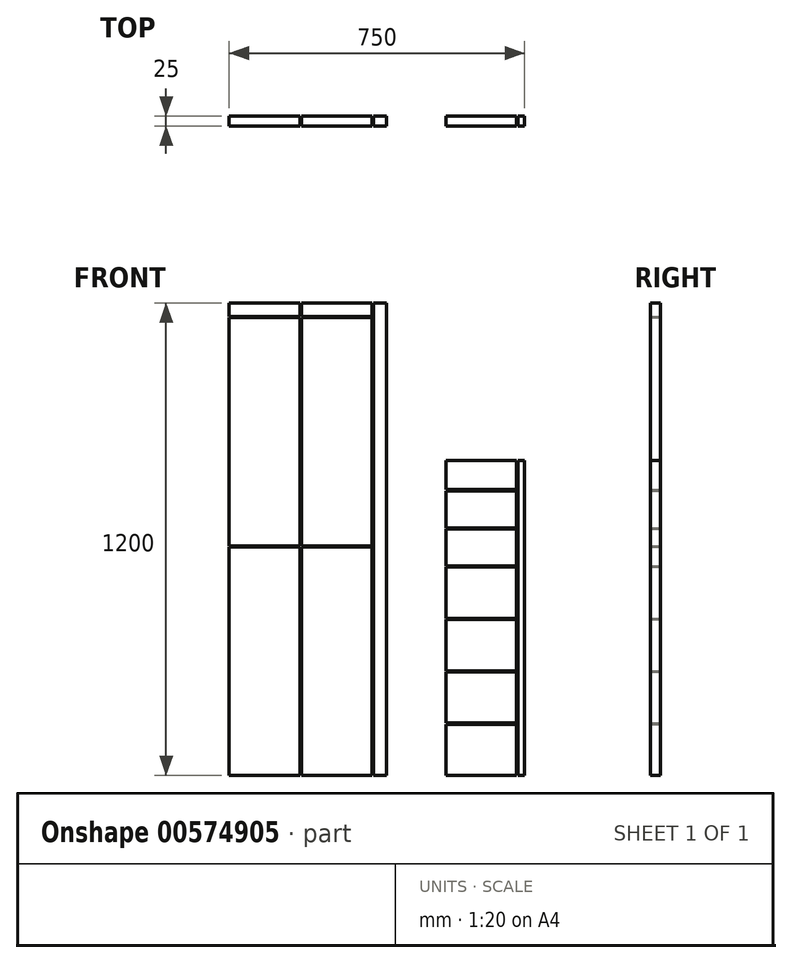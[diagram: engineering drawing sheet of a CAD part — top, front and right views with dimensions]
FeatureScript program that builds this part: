
annotation { "Feature Type Name" : "Feature", "Feature Type Description" : "" }
export const myFeature = defineFeature(function(context is Context, id is Id, definition is map)
    precondition{}
    {
        {
            var Q0;
            Q0=qCreatedBy(makeId("Front.planeOp"),FACE);
            var sketch = newSketch(context, id + "F0", { "sketchPlane" : qUnion([Q0])});
            skLineSegment(sketch, "E0.bottom", {"start": v(0, 0) * mm, "end": v(400, 0) * mm});
            skLineSegment(sketch, "E0.top", {"start": v(0, 1200) * mm, "end": v(400, 1200) * mm});
            skLineSegment(sketch, "E0.left", {"start": v(0, 0) * mm, "end": v(0, 1200) * mm});
            skLineSegment(sketch, "E0.right", {"start": v(400, 0) * mm, "end": v(400, 1200) * mm});
            skLineSegment(sketch, "E1", {"start": v(180, 0) * mm, "end": v(180, 1200) * mm});
            skLineSegment(sketch, "E2.0", {"start": v(183, 0) * mm, "end": v(183, 1200) * mm});
            skLineSegment(sketch, "E3.0", {"start": v(363, 0) * mm, "end": v(363, 1200) * mm});
            skLineSegment(sketch, "E4.0", {"start": v(366, 0) * mm, "end": v(366, 1200) * mm});
            skLineSegment(sketch, "E5", {"start": v(0, 580) * mm, "end": v(366, 580) * mm});
            skLineSegment(sketch, "E6.0", {"start": v(0, 583) * mm, "end": v(366, 583) * mm});
            skLineSegment(sketch, "E7.0", {"start": v(0, 1163) * mm, "end": v(366, 1163) * mm});
            skLineSegment(sketch, "E8.0", {"start": v(0, 1166) * mm, "end": v(366, 1166) * mm});
            skSolve(sketch);
        }
        {
            var Q0;
            {var subQ0=sQuery(id+"F0.wireOp",EDGE,"E6.0");var subQ1=sQuery(id+"F0.wireOp",EDGE,"E0.left");var subQ2=makeQuery(id+"F0.imprint","INTERSECT",VERTEX,{"derivedFrom":[subQ1,subQ0]});Q0=makeQuery(id+"F0.imprint","IMPRINT",FACE,{"disambiguationData":[TD([[makeQuery(id+"F0.imprint","IMPRINT",EDGE,{"disambiguationData":[TD([[subQ2,-1.0]])],"derivedFrom":subQ1}),-1.0]])]});}
            var Q1;
            {var subQ0=sQuery(id+"F0.wireOp",EDGE,"E6.0");var subQ1=sQuery(id+"F0.wireOp",EDGE,"E2.0");var subQ2=makeQuery(id+"F0.imprint","INTERSECT",VERTEX,{"derivedFrom":[subQ1,subQ0]});Q1=makeQuery(id+"F0.imprint","IMPRINT",FACE,{"disambiguationData":[TD([[makeQuery(id+"F0.imprint","IMPRINT",EDGE,{"disambiguationData":[TD([[subQ2,-1.0]])],"derivedFrom":subQ1}),-1.0]])]});}
            var Q2;
            {var subQ0=sQuery(id+"F0.wireOp",EDGE,"E0.left");var subQ1=sQuery(id+"F0.wireOp",EDGE,"E0.bottom");var subQ2=makeQuery(id+"F0.imprint","INTERSECT",VERTEX,{"derivedFrom":[subQ1,subQ0]});Q2=makeQuery(id+"F0.imprint","IMPRINT",FACE,{"disambiguationData":[TD([[makeQuery(id+"F0.imprint","IMPRINT",EDGE,{"disambiguationData":[TD([[subQ2,-1.0]])],"derivedFrom":subQ1}),1.0]])]});}
            var Q3;
            {var subQ0=sQuery(id+"F0.wireOp",EDGE,"E2.0");var subQ1=sQuery(id+"F0.wireOp",EDGE,"E0.bottom");var subQ2=makeQuery(id+"F0.imprint","INTERSECT",VERTEX,{"derivedFrom":[subQ1,subQ0]});Q3=makeQuery(id+"F0.imprint","IMPRINT",FACE,{"disambiguationData":[TD([[makeQuery(id+"F0.imprint","IMPRINT",EDGE,{"disambiguationData":[TD([[subQ2,-1.0]])],"derivedFrom":subQ1}),1.0]])]});}
            var Q4;
            {var subQ0=sQuery(id+"F0.wireOp",EDGE,"E0.left");var subQ1=sQuery(id+"F0.wireOp",EDGE,"E0.top");var subQ2=makeQuery(id+"F0.imprint","INTERSECT",VERTEX,{"derivedFrom":[subQ1,subQ0]});Q4=makeQuery(id+"F0.imprint","IMPRINT",FACE,{"disambiguationData":[TD([[makeQuery(id+"F0.imprint","IMPRINT",EDGE,{"disambiguationData":[TD([[subQ2,-1.0]])],"derivedFrom":subQ1}),-1.0]])]});}
            var Q5;
            {var subQ0=sQuery(id+"F0.wireOp",EDGE,"E2.0");var subQ1=sQuery(id+"F0.wireOp",EDGE,"E0.top");var subQ2=makeQuery(id+"F0.imprint","INTERSECT",VERTEX,{"derivedFrom":[subQ1,subQ0]});Q5=makeQuery(id+"F0.imprint","IMPRINT",FACE,{"disambiguationData":[TD([[makeQuery(id+"F0.imprint","IMPRINT",EDGE,{"disambiguationData":[TD([[subQ2,-1.0]])],"derivedFrom":subQ1}),-1.0]])]});}
            var Q6;
            {var subQ4=sQuery(id+"F0.wireOp",EDGE,"E0.right");Q6=makeQuery(id+"F0.imprint","IMPRINT",FACE,{"disambiguationData":[TD([[makeQuery(id+"F0.imprint","IMPRINT",EDGE,{"derivedFrom":subQ4}),1.0]])]});}
            extrude(context, id + "F1", {"entities" : qUnion([Q0, Q1, Q2, Q3, Q4, Q5, Q6]), "depth" : 25 * mm, "offsetDistance" : 25 * mm});
        }
        {
            var Q0;
            Q0=qCreatedBy(makeId("Front.planeOp"),FACE);
            var sketch = newSketch(context, id + "F2", { "sketchPlane" : qUnion([Q0])});
            skLineSegment(sketch, "E9.bottom", {"start": v(550, 0) * mm, "end": v(750, 0) * mm});
            skLineSegment(sketch, "E9.top", {"start": v(550, 800) * mm, "end": v(750, 800) * mm});
            skLineSegment(sketch, "E9.left", {"start": v(550, 0) * mm, "end": v(550, 800) * mm});
            skLineSegment(sketch, "E9.right", {"start": v(750, 0) * mm, "end": v(750, 800) * mm});
            skLineSegment(sketch, "E10.0", {"start": v(730, 0) * mm, "end": v(730, 800) * mm});
            skLineSegment(sketch, "E11", {"start": v(550, 130) * mm, "end": v(730, 130) * mm});
            skLineSegment(sketch, "E12.0", {"start": v(550, 133) * mm, "end": v(730, 133) * mm});
            skLineSegment(sketch, "E13.0", {"start": v(550, 263) * mm, "end": v(730, 263) * mm});
            skLineSegment(sketch, "E14.0", {"start": v(550, 266) * mm, "end": v(730, 266) * mm});
            skLineSegment(sketch, "E15.0", {"start": v(550, 396) * mm, "end": v(730, 396) * mm});
            skLineSegment(sketch, "E16.0", {"start": v(550, 399) * mm, "end": v(730, 399) * mm});
            skLineSegment(sketch, "E17.0", {"start": v(550, 529) * mm, "end": v(730, 529) * mm});
            skLineSegment(sketch, "E18.0", {"start": v(550, 532) * mm, "end": v(730, 532) * mm});
            skLineSegment(sketch, "E19.0", {"start": v(550, 626) * mm, "end": v(730, 626) * mm});
            skLineSegment(sketch, "E20.0", {"start": v(550, 629) * mm, "end": v(730, 629) * mm});
            skLineSegment(sketch, "E21.0", {"start": v(550, 723) * mm, "end": v(730, 723) * mm});
            skLineSegment(sketch, "E22.0", {"start": v(550, 726) * mm, "end": v(730, 726) * mm});
            skLineSegment(sketch, "E23.0", {"start": v(733, 0) * mm, "end": v(733, 800) * mm});
            skSolve(sketch);
        }
        {
            var Q0;
            {var subQ5=sQuery(id+"F2.wireOp",EDGE,"E11");Q0=makeQuery(id+"F2.imprint","IMPRINT",FACE,{"disambiguationData":[TD([[makeQuery(id+"F2.imprint","IMPRINT",EDGE,{"derivedFrom":subQ5}),-1.0]])]});}
            var Q1;
            {var subQ0=sQuery(id+"F2.wireOp",EDGE,"E12.0");Q1=makeQuery(id+"F2.imprint","IMPRINT",FACE,{"disambiguationData":[TD([[makeQuery(id+"F2.imprint","IMPRINT",EDGE,{"derivedFrom":subQ0}),1.0]])]});}
            var Q2;
            {var subQ0=sQuery(id+"F2.wireOp",EDGE,"E14.0");Q2=makeQuery(id+"F2.imprint","IMPRINT",FACE,{"disambiguationData":[TD([[makeQuery(id+"F2.imprint","IMPRINT",EDGE,{"derivedFrom":subQ0}),1.0]])]});}
            var Q3;
            {var subQ0=sQuery(id+"F2.wireOp",EDGE,"E16.0");Q3=makeQuery(id+"F2.imprint","IMPRINT",FACE,{"disambiguationData":[TD([[makeQuery(id+"F2.imprint","IMPRINT",EDGE,{"derivedFrom":subQ0}),1.0]])]});}
            var Q4;
            {var subQ0=sQuery(id+"F2.wireOp",EDGE,"E18.0");Q4=makeQuery(id+"F2.imprint","IMPRINT",FACE,{"disambiguationData":[TD([[makeQuery(id+"F2.imprint","IMPRINT",EDGE,{"derivedFrom":subQ0}),1.0]])]});}
            var Q5;
            {var subQ0=sQuery(id+"F2.wireOp",EDGE,"E20.0");Q5=makeQuery(id+"F2.imprint","IMPRINT",FACE,{"disambiguationData":[TD([[makeQuery(id+"F2.imprint","IMPRINT",EDGE,{"derivedFrom":subQ0}),1.0]])]});}
            var Q6;
            {var subQ5=sQuery(id+"F2.wireOp",EDGE,"E22.0");Q6=makeQuery(id+"F2.imprint","IMPRINT",FACE,{"disambiguationData":[TD([[makeQuery(id+"F2.imprint","IMPRINT",EDGE,{"derivedFrom":subQ5}),1.0]])]});}
            var Q7;
            {var subQ0=sQuery(id+"F2.wireOp",EDGE,"E9.right");Q7=makeQuery(id+"F2.imprint","IMPRINT",FACE,{"disambiguationData":[TD([[makeQuery(id+"F2.imprint","IMPRINT",EDGE,{"derivedFrom":subQ0}),1.0]])]});}
            extrude(context, id + "F3", {"entities" : qUnion([Q0, Q1, Q2, Q3, Q4, Q5, Q6, Q7]), "depth" : 25 * mm, "offsetDistance" : 25 * mm});
        }
    });
